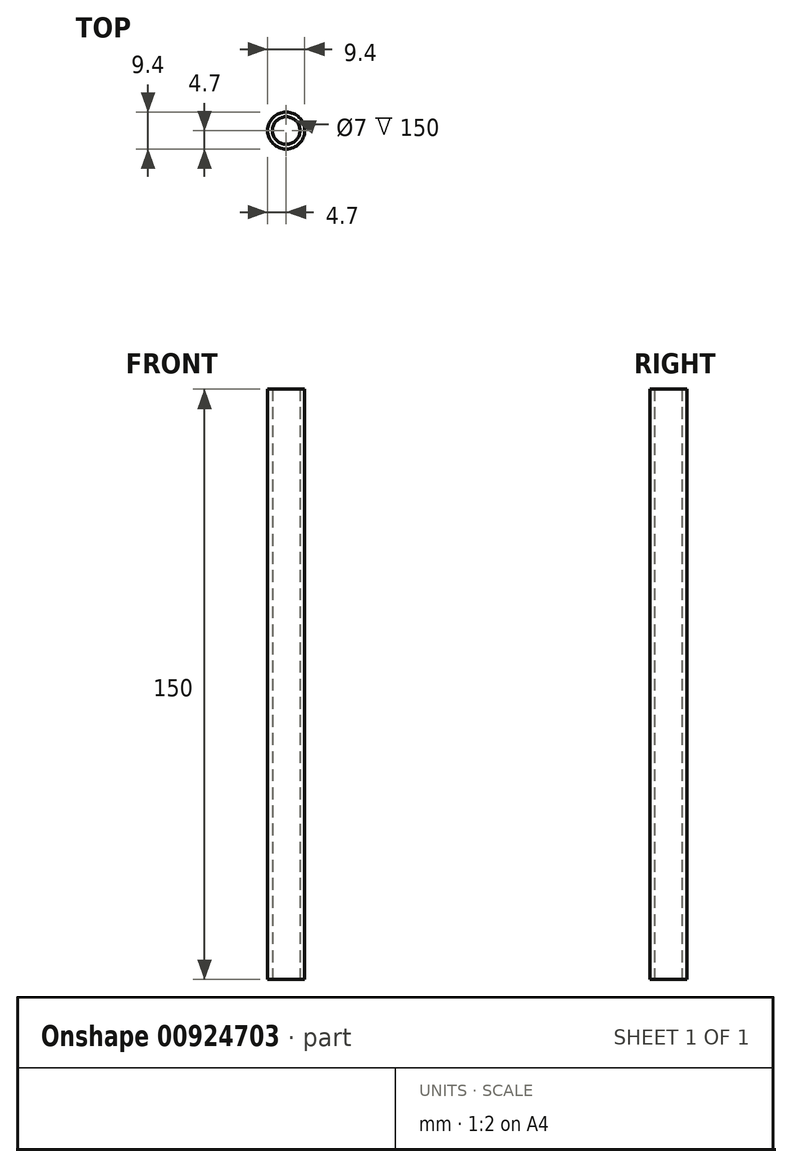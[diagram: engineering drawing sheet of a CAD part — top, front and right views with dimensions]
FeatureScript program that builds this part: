
annotation { "Feature Type Name" : "Feature", "Feature Type Description" : "" }
export const myFeature = defineFeature(function(context is Context, id is Id, definition is map)
    precondition{}
    {
        {
            var Q0;
            Q0=qCreatedBy(makeId("Top.planeOp"),FACE);
            var sketch = newSketch(context, id + "F0", { "sketchPlane" : qUnion([Q0])});
            skCircle(sketch, "E0", {"center": v(0, 0) * mm, "radius": 3.5 * mm});
            skCircle(sketch, "E1", {"center": v(0, 0) * mm, "radius": 4.7 * mm});
            skSolve(sketch);
        }
        {
            var Q0;
            Q0 = qSketchRegion(id + "F0", true);
            extrude(context, id + "F1", {"entities" : qUnion([Q0]), "depth" : 150 * mm, "offsetDistance" : 25 * mm});
        }
    });
